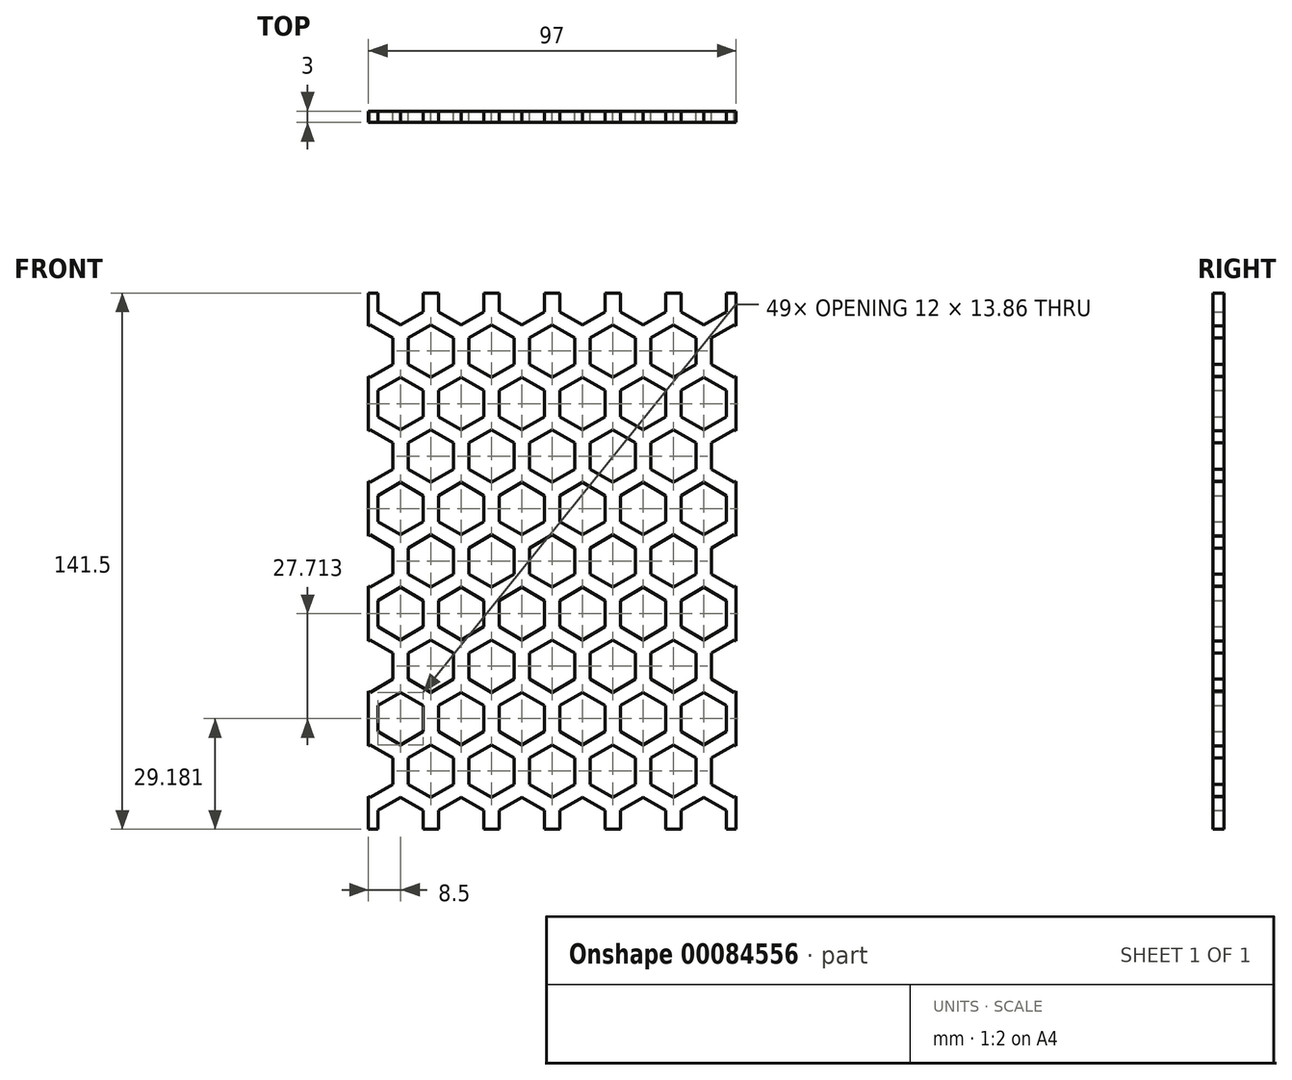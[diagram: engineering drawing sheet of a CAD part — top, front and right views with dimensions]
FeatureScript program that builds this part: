
annotation { "Feature Type Name" : "Feature", "Feature Type Description" : "" }
export const myFeature = defineFeature(function(context is Context, id is Id, definition is map)
    precondition{}
    {
        {
            var Q0;
            Q0=qCreatedBy(makeId("Front.planeOp"),FACE);
            var sketch = newSketch(context, id + "F0", { "sketchPlane" : qUnion([Q0]) });
            skLineSegment(sketch, "E0.bottom", {"start": v(48.5, -70.75) * mm, "end": v(-48.5, -70.75) * mm});
            skLineSegment(sketch, "E0.top", {"start": v(48.5, 70.75) * mm, "end": v(-48.5, 70.75) * mm});
            skLineSegment(sketch, "E0.left", {"start": v(48.5, -70.75) * mm, "end": v(48.5, 70.75) * mm});
            skLineSegment(sketch, "E0.right", {"start": v(-48.5, -70.75) * mm, "end": v(-48.5, 70.75) * mm});
            skPoint(sketch, "E0.middle", {"position": v(0, 0) * mm});
            skCircle(sketch, "E1.cCircle", {"center": v(0, 0) * mm, "radius": 6 * mm, "construction": true});
            skLineSegment(sketch, "E1.0", {"start": v(6, 3.46) * mm, "end": v(6, -3.46) * mm});
            skLineSegment(sketch, "E1.1", {"start": v(6, -3.46) * mm, "end": v(0, -6.93) * mm});
            skLineSegment(sketch, "E1.2", {"start": v(0, -6.93) * mm, "end": v(-6, -3.46) * mm});
            skLineSegment(sketch, "E1.3", {"start": v(-6, -3.46) * mm, "end": v(-6, 3.46) * mm});
            skLineSegment(sketch, "E1.4", {"start": v(-6, 3.46) * mm, "end": v(0, 6.93) * mm});
            skLineSegment(sketch, "E1.5", {"start": v(0, 6.93) * mm, "end": v(6, 3.46) * mm});
            skPoint(sketch, "E1.0.midPoint", {"position": v(6, 0) * mm});
            skLineSegment(sketch, "E2", {"start": v(0, 0) * mm, "end": v(8, 13.86) * mm, "construction": true});
            skCircle(sketch, "E3.cCircle", {"center": v(8, 13.86) * mm, "radius": 6 * mm, "construction": true});
            skLineSegment(sketch, "E3.0", {"start": v(14, 17.32) * mm, "end": v(14, 10.4) * mm});
            skLineSegment(sketch, "E3.1", {"start": v(14, 10.4) * mm, "end": v(8, 6.93) * mm});
            skLineSegment(sketch, "E3.2", {"start": v(8, 6.93) * mm, "end": v(2, 10.4) * mm});
            skLineSegment(sketch, "E3.3", {"start": v(2, 10.4) * mm, "end": v(2, 17.32) * mm});
            skLineSegment(sketch, "E3.4", {"start": v(2, 17.32) * mm, "end": v(8, 20.78) * mm});
            skLineSegment(sketch, "E3.5", {"start": v(8, 20.78) * mm, "end": v(14, 17.32) * mm});
            skPoint(sketch, "E3.0.midPoint", {"position": v(14, 13.86) * mm});
            skLineSegment(sketch, "E4.0.1.0", {"start": v(-6, 24.25) * mm, "end": v(-6, 31.18) * mm});
            skLineSegment(sketch, "E4.0.1.1", {"start": v(-6, 31.18) * mm, "end": v(0, 34.64) * mm});
            skLineSegment(sketch, "E4.0.1.2", {"start": v(0, 20.78) * mm, "end": v(-6, 24.25) * mm});
            skLineSegment(sketch, "E4.0.1.3", {"start": v(6, 24.25) * mm, "end": v(0, 20.78) * mm});
            skLineSegment(sketch, "E4.0.1.4", {"start": v(6, 31.18) * mm, "end": v(6, 24.25) * mm});
            skLineSegment(sketch, "E4.0.1.5", {"start": v(0, 34.64) * mm, "end": v(6, 31.18) * mm});
            skLineSegment(sketch, "E4.0.1.6", {"start": v(14, 38.1) * mm, "end": v(8, 34.64) * mm});
            skLineSegment(sketch, "E4.0.1.7", {"start": v(8, 34.64) * mm, "end": v(2, 38.1) * mm});
            skLineSegment(sketch, "E4.0.1.8", {"start": v(2, 38.1) * mm, "end": v(2, 45.03) * mm});
            skLineSegment(sketch, "E4.0.1.9", {"start": v(14, 45.03) * mm, "end": v(14, 38.1) * mm});
            skLineSegment(sketch, "E4.0.1.10", {"start": v(8, 48.5) * mm, "end": v(14, 45.03) * mm});
            skLineSegment(sketch, "E4.0.1.11", {"start": v(2, 45.03) * mm, "end": v(8, 48.5) * mm});
            skLineSegment(sketch, "E4.0.2.0", {"start": v(-6, 51.96) * mm, "end": v(-6, 58.89) * mm});
            skLineSegment(sketch, "E4.0.2.1", {"start": v(-6, 58.89) * mm, "end": v(0, 62.35) * mm});
            skLineSegment(sketch, "E4.0.2.2", {"start": v(0, 48.5) * mm, "end": v(-6, 51.96) * mm});
            skLineSegment(sketch, "E4.0.2.3", {"start": v(6, 51.96) * mm, "end": v(0, 48.5) * mm});
            skLineSegment(sketch, "E4.0.2.4", {"start": v(6, 58.89) * mm, "end": v(6, 51.96) * mm});
            skLineSegment(sketch, "E4.0.2.5", {"start": v(0, 62.35) * mm, "end": v(6, 58.89) * mm});
            skLineSegment(sketch, "E4.0.2.6", {"start": v(14, 65.82) * mm, "end": v(8, 62.35) * mm});
            skLineSegment(sketch, "E4.0.2.7", {"start": v(8, 62.35) * mm, "end": v(2, 65.82) * mm});
            skLineSegment(sketch, "E4.0.2.8", {"start": v(2, 65.82) * mm, "end": v(2, 72.75) * mm});
            skLineSegment(sketch, "E4.0.2.9", {"start": v(14, 72.75) * mm, "end": v(14, 65.82) * mm});
            skLineSegment(sketch, "E4.0.2.10", {"start": v(8, 76.21) * mm, "end": v(14, 72.75) * mm});
            skLineSegment(sketch, "E4.0.2.11", {"start": v(2, 72.75) * mm, "end": v(8, 76.21) * mm});
            skLineSegment(sketch, "E4.1.0.0", {"start": v(10, -3.46) * mm, "end": v(10, 3.46) * mm});
            skLineSegment(sketch, "E4.1.0.1", {"start": v(10, 3.46) * mm, "end": v(16, 6.93) * mm});
            skLineSegment(sketch, "E4.1.0.2", {"start": v(16, -6.93) * mm, "end": v(10, -3.46) * mm});
            skLineSegment(sketch, "E4.1.0.3", {"start": v(22, -3.46) * mm, "end": v(16, -6.93) * mm});
            skLineSegment(sketch, "E4.1.0.4", {"start": v(22, 3.46) * mm, "end": v(22, -3.46) * mm});
            skLineSegment(sketch, "E4.1.0.5", {"start": v(16, 6.93) * mm, "end": v(22, 3.46) * mm});
            skLineSegment(sketch, "E4.1.0.6", {"start": v(30, 10.4) * mm, "end": v(24, 6.93) * mm});
            skLineSegment(sketch, "E4.1.0.7", {"start": v(24, 6.93) * mm, "end": v(18, 10.4) * mm});
            skLineSegment(sketch, "E4.1.0.8", {"start": v(18, 10.4) * mm, "end": v(18, 17.32) * mm});
            skLineSegment(sketch, "E4.1.0.9", {"start": v(30, 17.32) * mm, "end": v(30, 10.4) * mm});
            skLineSegment(sketch, "E4.1.0.10", {"start": v(24, 20.78) * mm, "end": v(30, 17.32) * mm});
            skLineSegment(sketch, "E4.1.0.11", {"start": v(18, 17.32) * mm, "end": v(24, 20.78) * mm});
            skLineSegment(sketch, "E4.1.1.0", {"start": v(10, 24.25) * mm, "end": v(10, 31.18) * mm});
            skLineSegment(sketch, "E4.1.1.1", {"start": v(10, 31.18) * mm, "end": v(16, 34.64) * mm});
            skLineSegment(sketch, "E4.1.1.2", {"start": v(16, 20.78) * mm, "end": v(10, 24.25) * mm});
            skLineSegment(sketch, "E4.1.1.3", {"start": v(22, 24.25) * mm, "end": v(16, 20.78) * mm});
            skLineSegment(sketch, "E4.1.1.4", {"start": v(22, 31.18) * mm, "end": v(22, 24.25) * mm});
            skLineSegment(sketch, "E4.1.1.5", {"start": v(16, 34.64) * mm, "end": v(22, 31.18) * mm});
            skLineSegment(sketch, "E4.1.1.6", {"start": v(30, 38.1) * mm, "end": v(24, 34.64) * mm});
            skLineSegment(sketch, "E4.1.1.7", {"start": v(24, 34.64) * mm, "end": v(18, 38.1) * mm});
            skLineSegment(sketch, "E4.1.1.8", {"start": v(18, 38.1) * mm, "end": v(18, 45.03) * mm});
            skLineSegment(sketch, "E4.1.1.9", {"start": v(30, 45.03) * mm, "end": v(30, 38.1) * mm});
            skLineSegment(sketch, "E4.1.1.10", {"start": v(24, 48.5) * mm, "end": v(30, 45.03) * mm});
            skLineSegment(sketch, "E4.1.1.11", {"start": v(18, 45.03) * mm, "end": v(24, 48.5) * mm});
            skLineSegment(sketch, "E4.1.2.0", {"start": v(10, 51.96) * mm, "end": v(10, 58.89) * mm});
            skLineSegment(sketch, "E4.1.2.1", {"start": v(10, 58.89) * mm, "end": v(16, 62.35) * mm});
            skLineSegment(sketch, "E4.1.2.2", {"start": v(16, 48.5) * mm, "end": v(10, 51.96) * mm});
            skLineSegment(sketch, "E4.1.2.3", {"start": v(22, 51.96) * mm, "end": v(16, 48.5) * mm});
            skLineSegment(sketch, "E4.1.2.4", {"start": v(22, 58.89) * mm, "end": v(22, 51.96) * mm});
            skLineSegment(sketch, "E4.1.2.5", {"start": v(16, 62.35) * mm, "end": v(22, 58.89) * mm});
            skLineSegment(sketch, "E4.1.2.6", {"start": v(30, 65.82) * mm, "end": v(24, 62.35) * mm});
            skLineSegment(sketch, "E4.1.2.7", {"start": v(24, 62.35) * mm, "end": v(18, 65.82) * mm});
            skLineSegment(sketch, "E4.1.2.8", {"start": v(18, 65.82) * mm, "end": v(18, 72.75) * mm});
            skLineSegment(sketch, "E4.1.2.9", {"start": v(30, 72.75) * mm, "end": v(30, 65.82) * mm});
            skLineSegment(sketch, "E4.1.2.10", {"start": v(24, 76.21) * mm, "end": v(30, 72.75) * mm});
            skLineSegment(sketch, "E4.1.2.11", {"start": v(18, 72.75) * mm, "end": v(24, 76.21) * mm});
            skLineSegment(sketch, "E4.2.0.0", {"start": v(26, -3.46) * mm, "end": v(26, 3.46) * mm});
            skLineSegment(sketch, "E4.2.0.1", {"start": v(26, 3.46) * mm, "end": v(32, 6.93) * mm});
            skLineSegment(sketch, "E4.2.0.2", {"start": v(32, -6.93) * mm, "end": v(26, -3.46) * mm});
            skLineSegment(sketch, "E4.2.0.3", {"start": v(38, -3.46) * mm, "end": v(32, -6.93) * mm});
            skLineSegment(sketch, "E4.2.0.4", {"start": v(38, 3.46) * mm, "end": v(38, -3.46) * mm});
            skLineSegment(sketch, "E4.2.0.5", {"start": v(32, 6.93) * mm, "end": v(38, 3.46) * mm});
            skLineSegment(sketch, "E4.2.0.6", {"start": v(46, 10.4) * mm, "end": v(40, 6.93) * mm});
            skLineSegment(sketch, "E4.2.0.7", {"start": v(40, 6.93) * mm, "end": v(34, 10.4) * mm});
            skLineSegment(sketch, "E4.2.0.8", {"start": v(34, 10.4) * mm, "end": v(34, 17.32) * mm});
            skLineSegment(sketch, "E4.2.0.9", {"start": v(46, 17.32) * mm, "end": v(46, 10.4) * mm});
            skLineSegment(sketch, "E4.2.0.10", {"start": v(40, 20.78) * mm, "end": v(46, 17.32) * mm});
            skLineSegment(sketch, "E4.2.0.11", {"start": v(34, 17.32) * mm, "end": v(40, 20.78) * mm});
            skLineSegment(sketch, "E4.2.1.0", {"start": v(26, 24.25) * mm, "end": v(26, 31.18) * mm});
            skLineSegment(sketch, "E4.2.1.1", {"start": v(26, 31.18) * mm, "end": v(32, 34.64) * mm});
            skLineSegment(sketch, "E4.2.1.2", {"start": v(32, 20.78) * mm, "end": v(26, 24.25) * mm});
            skLineSegment(sketch, "E4.2.1.3", {"start": v(38, 24.25) * mm, "end": v(32, 20.78) * mm});
            skLineSegment(sketch, "E4.2.1.4", {"start": v(38, 31.18) * mm, "end": v(38, 24.25) * mm});
            skLineSegment(sketch, "E4.2.1.5", {"start": v(32, 34.64) * mm, "end": v(38, 31.18) * mm});
            skLineSegment(sketch, "E4.2.1.6", {"start": v(46, 38.1) * mm, "end": v(40, 34.64) * mm});
            skLineSegment(sketch, "E4.2.1.7", {"start": v(40, 34.64) * mm, "end": v(34, 38.1) * mm});
            skLineSegment(sketch, "E4.2.1.8", {"start": v(34, 38.1) * mm, "end": v(34, 45.03) * mm});
            skLineSegment(sketch, "E4.2.1.9", {"start": v(46, 45.03) * mm, "end": v(46, 38.1) * mm});
            skLineSegment(sketch, "E4.2.1.10", {"start": v(40, 48.5) * mm, "end": v(46, 45.03) * mm});
            skLineSegment(sketch, "E4.2.1.11", {"start": v(34, 45.03) * mm, "end": v(40, 48.5) * mm});
            skLineSegment(sketch, "E4.2.2.0", {"start": v(26, 51.96) * mm, "end": v(26, 58.89) * mm});
            skLineSegment(sketch, "E4.2.2.1", {"start": v(26, 58.89) * mm, "end": v(32, 62.35) * mm});
            skLineSegment(sketch, "E4.2.2.2", {"start": v(32, 48.5) * mm, "end": v(26, 51.96) * mm});
            skLineSegment(sketch, "E4.2.2.3", {"start": v(38, 51.96) * mm, "end": v(32, 48.5) * mm});
            skLineSegment(sketch, "E4.2.2.4", {"start": v(38, 58.89) * mm, "end": v(38, 51.96) * mm});
            skLineSegment(sketch, "E4.2.2.5", {"start": v(32, 62.35) * mm, "end": v(38, 58.89) * mm});
            skLineSegment(sketch, "E4.2.2.6", {"start": v(46, 65.82) * mm, "end": v(40, 62.35) * mm});
            skLineSegment(sketch, "E4.2.2.7", {"start": v(40, 62.35) * mm, "end": v(34, 65.82) * mm});
            skLineSegment(sketch, "E4.2.2.8", {"start": v(34, 65.82) * mm, "end": v(34, 72.75) * mm});
            skLineSegment(sketch, "E4.2.2.9", {"start": v(46, 72.75) * mm, "end": v(46, 65.82) * mm});
            skLineSegment(sketch, "E4.2.2.10", {"start": v(40, 76.21) * mm, "end": v(46, 72.75) * mm});
            skLineSegment(sketch, "E4.2.2.11", {"start": v(34, 72.75) * mm, "end": v(40, 76.21) * mm});
            skLineSegment(sketch, "E4.3.0.0", {"start": v(42, -3.46) * mm, "end": v(42, 3.46) * mm});
            skLineSegment(sketch, "E4.3.0.1", {"start": v(42, 3.46) * mm, "end": v(48, 6.93) * mm});
            skLineSegment(sketch, "E4.3.0.2", {"start": v(48, -6.93) * mm, "end": v(42, -3.46) * mm});
            skLineSegment(sketch, "E4.3.0.3", {"start": v(54, -3.46) * mm, "end": v(48, -6.93) * mm});
            skLineSegment(sketch, "E4.3.0.4", {"start": v(54, 3.46) * mm, "end": v(54, -3.46) * mm});
            skLineSegment(sketch, "E4.3.0.5", {"start": v(48, 6.93) * mm, "end": v(54, 3.46) * mm});
            skLineSegment(sketch, "E4.3.0.6", {"start": v(62, 10.4) * mm, "end": v(56, 6.93) * mm});
            skLineSegment(sketch, "E4.3.0.7", {"start": v(56, 6.93) * mm, "end": v(50, 10.4) * mm});
            skLineSegment(sketch, "E4.3.0.8", {"start": v(50, 10.4) * mm, "end": v(50, 17.32) * mm});
            skLineSegment(sketch, "E4.3.0.9", {"start": v(62, 17.32) * mm, "end": v(62, 10.4) * mm});
            skLineSegment(sketch, "E4.3.0.10", {"start": v(56, 20.78) * mm, "end": v(62, 17.32) * mm});
            skLineSegment(sketch, "E4.3.0.11", {"start": v(50, 17.32) * mm, "end": v(56, 20.78) * mm});
            skLineSegment(sketch, "E4.3.1.0", {"start": v(42, 24.25) * mm, "end": v(42, 31.18) * mm});
            skLineSegment(sketch, "E4.3.1.1", {"start": v(42, 31.18) * mm, "end": v(48, 34.64) * mm});
            skLineSegment(sketch, "E4.3.1.2", {"start": v(48, 20.78) * mm, "end": v(42, 24.25) * mm});
            skLineSegment(sketch, "E4.3.1.3", {"start": v(54, 24.25) * mm, "end": v(48, 20.78) * mm});
            skLineSegment(sketch, "E4.3.1.4", {"start": v(54, 31.18) * mm, "end": v(54, 24.25) * mm});
            skLineSegment(sketch, "E4.3.1.5", {"start": v(48, 34.64) * mm, "end": v(54, 31.18) * mm});
            skLineSegment(sketch, "E4.3.1.6", {"start": v(62, 38.1) * mm, "end": v(56, 34.64) * mm});
            skLineSegment(sketch, "E4.3.1.7", {"start": v(56, 34.64) * mm, "end": v(50, 38.1) * mm});
            skLineSegment(sketch, "E4.3.1.8", {"start": v(50, 38.1) * mm, "end": v(50, 45.03) * mm});
            skLineSegment(sketch, "E4.3.1.9", {"start": v(62, 45.03) * mm, "end": v(62, 38.1) * mm});
            skLineSegment(sketch, "E4.3.1.10", {"start": v(56, 48.5) * mm, "end": v(62, 45.03) * mm});
            skLineSegment(sketch, "E4.3.1.11", {"start": v(50, 45.03) * mm, "end": v(56, 48.5) * mm});
            skLineSegment(sketch, "E4.3.2.0", {"start": v(42, 51.96) * mm, "end": v(42, 58.89) * mm});
            skLineSegment(sketch, "E4.3.2.1", {"start": v(42, 58.89) * mm, "end": v(48, 62.35) * mm});
            skLineSegment(sketch, "E4.3.2.2", {"start": v(48, 48.5) * mm, "end": v(42, 51.96) * mm});
            skLineSegment(sketch, "E4.3.2.3", {"start": v(54, 51.96) * mm, "end": v(48, 48.5) * mm});
            skLineSegment(sketch, "E4.3.2.4", {"start": v(54, 58.89) * mm, "end": v(54, 51.96) * mm});
            skLineSegment(sketch, "E4.3.2.5", {"start": v(48, 62.35) * mm, "end": v(54, 58.89) * mm});
            skLineSegment(sketch, "E4.3.2.6", {"start": v(62, 65.82) * mm, "end": v(56, 62.35) * mm});
            skLineSegment(sketch, "E4.3.2.7", {"start": v(56, 62.35) * mm, "end": v(50, 65.82) * mm});
            skLineSegment(sketch, "E4.3.2.8", {"start": v(50, 65.82) * mm, "end": v(50, 72.75) * mm});
            skLineSegment(sketch, "E4.3.2.9", {"start": v(62, 72.75) * mm, "end": v(62, 65.82) * mm});
            skLineSegment(sketch, "E4.3.2.10", {"start": v(56, 76.21) * mm, "end": v(62, 72.75) * mm});
            skLineSegment(sketch, "E4.3.2.11", {"start": v(50, 72.75) * mm, "end": v(56, 76.21) * mm});
            skLineSegment(sketch, "E4.direction1", {"start": v(-6, -3.46) * mm, "end": v(10, -3.46) * mm, "construction": true});
            skLineSegment(sketch, "E4.direction2", {"start": v(-6, -3.46) * mm, "end": v(-6, 24.25) * mm, "construction": true});
            skLineSegment(sketch, "E5.MirrorCS", {"start": v(-32, 20.78) * mm, "end": v(-26, 24.25) * mm});
            skLineSegment(sketch, "E6.MirrorCS", {"start": v(-48, 20.78) * mm, "end": v(-42, 24.25) * mm});
            skLineSegment(sketch, "E7.MirrorCS", {"start": v(-2, 45.03) * mm, "end": v(-8, 48.5) * mm});
            skLineSegment(sketch, "E8.MirrorCS", {"start": v(-22, -3.46) * mm, "end": v(-16, -6.93) * mm});
            skLineSegment(sketch, "E9.MirrorCS", {"start": v(-18, 72.75) * mm, "end": v(-24, 76.21) * mm});
            skLineSegment(sketch, "E10.MirrorCS", {"start": v(-38, 24.25) * mm, "end": v(-32, 20.78) * mm});
            skLineSegment(sketch, "E11.MirrorCS", {"start": v(-40, 34.64) * mm, "end": v(-34, 38.1) * mm});
            skLineSegment(sketch, "E12.MirrorCS", {"start": v(-34, 72.75) * mm, "end": v(-40, 76.21) * mm});
            skLineSegment(sketch, "E13.MirrorCS", {"start": v(-24, 6.93) * mm, "end": v(-18, 10.4) * mm});
            skLineSegment(sketch, "E14.MirrorCS", {"start": v(-48, 34.64) * mm, "end": v(-54, 31.18) * mm});
            skLineSegment(sketch, "E15.MirrorCS", {"start": v(0, 62.35) * mm, "end": v(-6, 58.89) * mm});
            skLineSegment(sketch, "E16.MirrorCS", {"start": v(-62, 38.1) * mm, "end": v(-56, 34.64) * mm});
            skLineSegment(sketch, "E17.MirrorCS", {"start": v(-48, -6.93) * mm, "end": v(-42, -3.46) * mm});
            skLineSegment(sketch, "E18.MirrorCS", {"start": v(-18, 17.32) * mm, "end": v(-24, 20.78) * mm});
            skLineSegment(sketch, "E19.MirrorCS", {"start": v(-22, 51.96) * mm, "end": v(-16, 48.5) * mm});
            skLineSegment(sketch, "E20.MirrorCS", {"start": v(-6, 24.25) * mm, "end": v(0, 20.78) * mm});
            skLineSegment(sketch, "E21.MirrorCS", {"start": v(-34, 45.03) * mm, "end": v(-40, 48.5) * mm});
            skLineSegment(sketch, "E22.MirrorCS", {"start": v(-10, 31.18) * mm, "end": v(-16, 34.64) * mm});
            skLineSegment(sketch, "E23.MirrorCS", {"start": v(-16, 62.35) * mm, "end": v(-22, 58.89) * mm});
            skLineSegment(sketch, "E24.MirrorCS", {"start": v(-26, 58.89) * mm, "end": v(-32, 62.35) * mm});
            skLineSegment(sketch, "E25.MirrorCS", {"start": v(-16, 20.78) * mm, "end": v(-10, 24.25) * mm});
            skLineSegment(sketch, "E26.MirrorCS", {"start": v(-62, 10.4) * mm, "end": v(-56, 6.93) * mm});
            skLineSegment(sketch, "E27.MirrorCS", {"start": v(-8, 34.64) * mm, "end": v(-2, 38.1) * mm});
            skLineSegment(sketch, "E28.MirrorCS", {"start": v(-2, 72.75) * mm, "end": v(-8, 76.21) * mm});
            skLineSegment(sketch, "E29.MirrorCS", {"start": v(-10, 3.46) * mm, "end": v(-16, 6.93) * mm});
            skLineSegment(sketch, "E30.MirrorCS", {"start": v(-16, 34.64) * mm, "end": v(-22, 31.18) * mm});
            skLineSegment(sketch, "E31.MirrorCS", {"start": v(-26, 31.18) * mm, "end": v(-32, 34.64) * mm});
            skLineSegment(sketch, "E32.MirrorCS", {"start": v(-24, 62.35) * mm, "end": v(-18, 65.82) * mm});
            skLineSegment(sketch, "E33.MirrorCS", {"start": v(-34, 17.32) * mm, "end": v(-40, 20.78) * mm});
            skLineSegment(sketch, "E34.MirrorCS", {"start": v(-42, 58.89) * mm, "end": v(-48, 62.35) * mm});
            skLineSegment(sketch, "E35.MirrorCS", {"start": v(-32, 62.35) * mm, "end": v(-38, 58.89) * mm});
            skLineSegment(sketch, "E36.MirrorCS", {"start": v(-22, 24.25) * mm, "end": v(-16, 20.78) * mm});
            skLineSegment(sketch, "E37.MirrorCS", {"start": v(-8, 6.93) * mm, "end": v(-2, 10.4) * mm});
            skLineSegment(sketch, "E38.MirrorCS", {"start": v(-42, 31.18) * mm, "end": v(-48, 34.64) * mm});
            skLineSegment(sketch, "E39.MirrorCS", {"start": v(-40, 62.35) * mm, "end": v(-34, 65.82) * mm});
            skLineSegment(sketch, "E40.MirrorCS", {"start": v(-2, 17.32) * mm, "end": v(-8, 20.78) * mm});
            skLineSegment(sketch, "E41.MirrorCS", {"start": v(-10, 58.89) * mm, "end": v(-16, 62.35) * mm});
            skLineSegment(sketch, "E42.MirrorCS", {"start": v(-32, 6.93) * mm, "end": v(-38, 3.46) * mm});
            skLineSegment(sketch, "E43.MirrorCS", {"start": v(-48, 62.35) * mm, "end": v(-54, 58.89) * mm});
            skLineSegment(sketch, "E44.MirrorCS", {"start": v(-48, 6.93) * mm, "end": v(-54, 3.46) * mm});
            skLineSegment(sketch, "E45.MirrorCS", {"start": v(-62, 65.82) * mm, "end": v(-56, 62.35) * mm});
            skLineSegment(sketch, "E46.MirrorCS", {"start": v(-38, -3.46) * mm, "end": v(-32, -6.93) * mm});
            skLineSegment(sketch, "E47.MirrorCS", {"start": v(-6, -3.46) * mm, "end": v(0, -6.93) * mm});
            skLineSegment(sketch, "E48.MirrorCS", {"start": v(-56, 48.5) * mm, "end": v(-62, 45.03) * mm});
            skLineSegment(sketch, "E49.MirrorCS", {"start": v(-32, 48.5) * mm, "end": v(-26, 51.96) * mm});
            skLineSegment(sketch, "E50.MirrorCS", {"start": v(-38, 51.96) * mm, "end": v(-32, 48.5) * mm});
            skLineSegment(sketch, "E51.MirrorCS", {"start": v(0, 34.64) * mm, "end": v(-6, 31.18) * mm});
            skLineSegment(sketch, "E52.MirrorCS", {"start": v(-54, -3.46) * mm, "end": v(-48, -6.93) * mm});
            skLineSegment(sketch, "E53.MirrorCS", {"start": v(-16, 48.5) * mm, "end": v(-10, 51.96) * mm});
            skLineSegment(sketch, "E54.MirrorCS", {"start": v(-56, 76.21) * mm, "end": v(-62, 72.75) * mm});
            skLineSegment(sketch, "E55.MirrorCS", {"start": v(-42, 3.46) * mm, "end": v(-48, 6.93) * mm});
            skLineSegment(sketch, "E56.MirrorCS", {"start": v(-8, 62.35) * mm, "end": v(-2, 65.82) * mm});
            skLineSegment(sketch, "E57.MirrorCS", {"start": v(-40, 6.93) * mm, "end": v(-34, 10.4) * mm});
            skLineSegment(sketch, "E58.MirrorCS", {"start": v(-50, 65.82) * mm, "end": v(-50, 72.75) * mm});
            skLineSegment(sketch, "E59.MirrorCS", {"start": v(-54, 24.25) * mm, "end": v(-48, 20.78) * mm});
            skLineSegment(sketch, "E60.MirrorCS", {"start": v(-6, 51.96) * mm, "end": v(0, 48.5) * mm});
            skLineSegment(sketch, "E61.MirrorCS", {"start": v(-18, 45.03) * mm, "end": v(-24, 48.5) * mm});
            skLineSegment(sketch, "E62.MirrorCS", {"start": v(-54, 51.96) * mm, "end": v(-48, 48.5) * mm});
            skLineSegment(sketch, "E63.MirrorCS", {"start": v(-24, 34.64) * mm, "end": v(-18, 38.1) * mm});
            skLineSegment(sketch, "E64.MirrorCS", {"start": v(-32, -6.93) * mm, "end": v(-26, -3.46) * mm});
            skLineSegment(sketch, "E65.MirrorCS", {"start": v(-26, 3.46) * mm, "end": v(-32, 6.93) * mm});
            skLineSegment(sketch, "E66.MirrorCS", {"start": v(-32, 34.64) * mm, "end": v(-38, 31.18) * mm});
            skLineSegment(sketch, "E67.MirrorCS", {"start": v(-56, 20.78) * mm, "end": v(-62, 17.32) * mm});
            skLineSegment(sketch, "E68.MirrorCS", {"start": v(-48, 48.5) * mm, "end": v(-42, 51.96) * mm});
            skLineSegment(sketch, "E69.MirrorCS", {"start": v(-16, -6.93) * mm, "end": v(-10, -3.46) * mm});
            skLineSegment(sketch, "E70.MirrorCS", {"start": v(-16, 6.93) * mm, "end": v(-22, 3.46) * mm});
            skLineSegment(sketch, "E71.MirrorCS", {"start": v(0, 6.93) * mm, "end": v(-6, 3.46) * mm});
            skLineSegment(sketch, "E72.MirrorCS", {"start": v(0, 0) * mm, "end": v(-8, 13.86) * mm, "construction": true});
            skLineSegment(sketch, "E73.MirrorCS", {"start": v(-6, 3.46) * mm, "end": v(-6, -3.46) * mm});
            skLineSegment(sketch, "E74.MirrorCS", {"start": v(-14, 10.4) * mm, "end": v(-8, 6.93) * mm});
            skLineSegment(sketch, "E75.MirrorCS", {"start": v(-14, 17.32) * mm, "end": v(-14, 10.4) * mm});
            skLineSegment(sketch, "E76.MirrorCS", {"start": v(-2, 10.4) * mm, "end": v(-2, 17.32) * mm});
            skCircle(sketch, "E77.MirrorC", {"center": v(-8, 13.86) * mm, "radius": 6 * mm, "construction": true});
            skLineSegment(sketch, "E78.MirrorCS", {"start": v(-46, 65.82) * mm, "end": v(-40, 62.35) * mm});
            skLineSegment(sketch, "E79.MirrorCS", {"start": v(-8, 48.5) * mm, "end": v(-14, 45.03) * mm});
            skLineSegment(sketch, "E80.MirrorCS", {"start": v(-30, 38.1) * mm, "end": v(-24, 34.64) * mm});
            skLineSegment(sketch, "E81.MirrorCS", {"start": v(-24, 76.21) * mm, "end": v(-30, 72.75) * mm});
            skLineSegment(sketch, "E82.MirrorCS", {"start": v(-46, 72.75) * mm, "end": v(-46, 65.82) * mm});
            skLineSegment(sketch, "E83.MirrorCS", {"start": v(-30, 45.03) * mm, "end": v(-30, 38.1) * mm});
            skPoint(sketch, "E84.MirrorP", {"position": v(-6, 0) * mm});
            skLineSegment(sketch, "E85.MirrorCS", {"start": v(-24, 48.5) * mm, "end": v(-30, 45.03) * mm});
            skLineSegment(sketch, "E86.MirrorCS", {"start": v(-46, 38.1) * mm, "end": v(-40, 34.64) * mm});
            skLineSegment(sketch, "E87.MirrorCS", {"start": v(-8, 20.78) * mm, "end": v(-14, 17.32) * mm});
            skLineSegment(sketch, "E88.MirrorCS", {"start": v(-56, 62.35) * mm, "end": v(-50, 65.82) * mm});
            skLineSegment(sketch, "E89.MirrorCS", {"start": v(-24, 20.78) * mm, "end": v(-30, 17.32) * mm});
            skLineSegment(sketch, "E90.MirrorCS", {"start": v(-50, 72.75) * mm, "end": v(-56, 76.21) * mm});
            skLineSegment(sketch, "E91.MirrorCS", {"start": v(-18, 10.4) * mm, "end": v(-18, 17.32) * mm});
            skLineSegment(sketch, "E92.MirrorCS", {"start": v(-54, 31.18) * mm, "end": v(-54, 24.25) * mm});
            skLineSegment(sketch, "E93.MirrorCS", {"start": v(-6, 31.18) * mm, "end": v(-6, 24.25) * mm});
            skLineSegment(sketch, "E94.MirrorCS", {"start": v(-10, 24.25) * mm, "end": v(-10, 31.18) * mm});
            skLineSegment(sketch, "E95.MirrorCS", {"start": v(-22, 58.89) * mm, "end": v(-22, 51.96) * mm});
            skLineSegment(sketch, "E96.MirrorCS", {"start": v(-26, 51.96) * mm, "end": v(-26, 58.89) * mm});
            skLineSegment(sketch, "E97.MirrorCS", {"start": v(-62, 45.03) * mm, "end": v(-62, 38.1) * mm});
            skLineSegment(sketch, "E98.MirrorCS", {"start": v(-8, 76.21) * mm, "end": v(-14, 72.75) * mm});
            skLineSegment(sketch, "E99.MirrorCS", {"start": v(-30, 65.82) * mm, "end": v(-24, 62.35) * mm});
            skLineSegment(sketch, "E100.MirrorCS", {"start": v(-14, 45.03) * mm, "end": v(-14, 38.1) * mm});
            skLineSegment(sketch, "E101.MirrorCS", {"start": v(-62, 17.32) * mm, "end": v(-62, 10.4) * mm});
            skLineSegment(sketch, "E102.MirrorCS", {"start": v(-30, 72.75) * mm, "end": v(-30, 65.82) * mm});
            skLineSegment(sketch, "E103.MirrorCS", {"start": v(-22, 31.18) * mm, "end": v(-22, 24.25) * mm});
            skLineSegment(sketch, "E104.MirrorCS", {"start": v(-38, 58.89) * mm, "end": v(-38, 51.96) * mm});
            skLineSegment(sketch, "E105.MirrorCS", {"start": v(-50, 10.4) * mm, "end": v(-50, 17.32) * mm});
            skLineSegment(sketch, "E106.MirrorCS", {"start": v(-2, 38.1) * mm, "end": v(-2, 45.03) * mm});
            skLineSegment(sketch, "E107.MirrorCS", {"start": v(-10, -3.46) * mm, "end": v(-10, 3.46) * mm});
            skLineSegment(sketch, "E108.MirrorCS", {"start": v(-42, 51.96) * mm, "end": v(-42, 58.89) * mm});
            skLineSegment(sketch, "E109.MirrorCS", {"start": v(-18, 65.82) * mm, "end": v(-18, 72.75) * mm});
            skLineSegment(sketch, "E110.MirrorCS", {"start": v(-50, 45.03) * mm, "end": v(-56, 48.5) * mm});
            skLineSegment(sketch, "E111.MirrorCS", {"start": v(-30, 17.32) * mm, "end": v(-30, 10.4) * mm});
            skLineSegment(sketch, "E112.MirrorCS", {"start": v(-46, 45.03) * mm, "end": v(-46, 38.1) * mm});
            skLineSegment(sketch, "E113.MirrorCS", {"start": v(-34, 65.82) * mm, "end": v(-34, 72.75) * mm});
            skLineSegment(sketch, "E114.MirrorCS", {"start": v(-54, 58.89) * mm, "end": v(-54, 51.96) * mm});
            skLineSegment(sketch, "E115.MirrorCS", {"start": v(-42, 24.25) * mm, "end": v(-42, 31.18) * mm});
            skLineSegment(sketch, "E116.MirrorCS", {"start": v(-26, -3.46) * mm, "end": v(-26, 3.46) * mm});
            skLineSegment(sketch, "E117.MirrorCS", {"start": v(-50, 38.1) * mm, "end": v(-50, 45.03) * mm});
            skLineSegment(sketch, "E118.MirrorCS", {"start": v(-42, -3.46) * mm, "end": v(-42, 3.46) * mm});
            skLineSegment(sketch, "E119.MirrorCS", {"start": v(-46, 10.4) * mm, "end": v(-40, 6.93) * mm});
            skLineSegment(sketch, "E120.MirrorCS", {"start": v(-6, 58.89) * mm, "end": v(-6, 51.96) * mm});
            skLineSegment(sketch, "E121.MirrorCS", {"start": v(-38, 3.46) * mm, "end": v(-38, -3.46) * mm});
            skLineSegment(sketch, "E122.MirrorCS", {"start": v(-38, 31.18) * mm, "end": v(-38, 24.25) * mm});
            skLineSegment(sketch, "E123.MirrorCS", {"start": v(-22, 3.46) * mm, "end": v(-22, -3.46) * mm});
            skLineSegment(sketch, "E124.MirrorCS", {"start": v(-50, 17.32) * mm, "end": v(-56, 20.78) * mm});
            skLineSegment(sketch, "E125.MirrorCS", {"start": v(-54, 3.46) * mm, "end": v(-54, -3.46) * mm});
            skLineSegment(sketch, "E126.MirrorCS", {"start": v(-46, 17.32) * mm, "end": v(-46, 10.4) * mm});
            skLineSegment(sketch, "E127.MirrorCS", {"start": v(-2, 65.82) * mm, "end": v(-2, 72.75) * mm});
            skLineSegment(sketch, "E128.MirrorCS", {"start": v(-40, 76.21) * mm, "end": v(-46, 72.75) * mm});
            skLineSegment(sketch, "E129.MirrorCS", {"start": v(-40, 20.78) * mm, "end": v(-46, 17.32) * mm});
            skLineSegment(sketch, "E130.MirrorCS", {"start": v(-14, 38.1) * mm, "end": v(-8, 34.64) * mm});
            skLineSegment(sketch, "E131.MirrorCS", {"start": v(-56, 6.93) * mm, "end": v(-50, 10.4) * mm});
            skLineSegment(sketch, "E132.MirrorCS", {"start": v(-14, 72.75) * mm, "end": v(-14, 65.82) * mm});
            skLineSegment(sketch, "E133.MirrorCS", {"start": v(-34, 10.4) * mm, "end": v(-34, 17.32) * mm});
            skLineSegment(sketch, "E134.MirrorCS", {"start": v(-34, 38.1) * mm, "end": v(-34, 45.03) * mm});
            skLineSegment(sketch, "E135.MirrorCS", {"start": v(-10, 51.96) * mm, "end": v(-10, 58.89) * mm});
            skLineSegment(sketch, "E136.MirrorCS", {"start": v(-40, 48.5) * mm, "end": v(-46, 45.03) * mm});
            skLineSegment(sketch, "E137.MirrorCS", {"start": v(-62, 72.75) * mm, "end": v(-62, 65.82) * mm});
            skLineSegment(sketch, "E138.MirrorCS", {"start": v(-56, 34.64) * mm, "end": v(-50, 38.1) * mm});
            skPoint(sketch, "E139.MirrorP", {"position": v(-14, 13.86) * mm});
            skLineSegment(sketch, "E140.MirrorCS", {"start": v(-18, 38.1) * mm, "end": v(-18, 45.03) * mm});
            skLineSegment(sketch, "E141.MirrorCS", {"start": v(-30, 10.4) * mm, "end": v(-24, 6.93) * mm});
            skLineSegment(sketch, "E142.MirrorCS", {"start": v(-26, 24.25) * mm, "end": v(-26, 31.18) * mm});
            skLineSegment(sketch, "E143.MirrorCS", {"start": v(-14, 65.82) * mm, "end": v(-8, 62.35) * mm});
            skLineSegment(sketch, "E144.MirrorCS", {"start": v(0, -20.78) * mm, "end": v(-6, -24.25) * mm});
            skLineSegment(sketch, "E145.MirrorCS", {"start": v(-6, -31.18) * mm, "end": v(0, -34.64) * mm});
            skLineSegment(sketch, "E146.MirrorCS", {"start": v(-6, -51.96) * mm, "end": v(0, -48.5) * mm});
            skLineSegment(sketch, "E147.MirrorCS", {"start": v(-6, -58.89) * mm, "end": v(0, -62.35) * mm});
            skLineSegment(sketch, "E148.MirrorCS", {"start": v(0, -62.35) * mm, "end": v(-6, -58.89) * mm});
            skLineSegment(sketch, "E149.MirrorCS", {"start": v(0, -48.5) * mm, "end": v(-6, -51.96) * mm});
            skLineSegment(sketch, "E150.MirrorCS", {"start": v(-6, -24.25) * mm, "end": v(0, -20.78) * mm});
            skLineSegment(sketch, "E151.MirrorCS", {"start": v(0, -34.64) * mm, "end": v(-6, -31.18) * mm});
            skLineSegment(sketch, "E152.MirrorCS", {"start": v(56, -20.78) * mm, "end": v(62, -17.32) * mm});
            skLineSegment(sketch, "E153.MirrorCS", {"start": v(30, -38.1) * mm, "end": v(24, -34.64) * mm});
            skLineSegment(sketch, "E154.MirrorCS", {"start": v(24, -76.21) * mm, "end": v(30, -72.75) * mm});
            skLineSegment(sketch, "E155.MirrorCS", {"start": v(14, -10.4) * mm, "end": v(8, -6.93) * mm});
            skLineSegment(sketch, "E156.MirrorCS", {"start": v(-14, -38.1) * mm, "end": v(-8, -34.64) * mm});
            skLineSegment(sketch, "E157.MirrorCS", {"start": v(56, -76.21) * mm, "end": v(62, -72.75) * mm});
            skLineSegment(sketch, "E158.MirrorCS", {"start": v(40, -48.5) * mm, "end": v(46, -45.03) * mm});
            skLineSegment(sketch, "E159.MirrorCS", {"start": v(46, -10.4) * mm, "end": v(40, -6.93) * mm});
            skLineSegment(sketch, "E160.MirrorCS", {"start": v(14, -65.82) * mm, "end": v(8, -62.35) * mm});
            skLineSegment(sketch, "E161.MirrorCS", {"start": v(-8, -48.5) * mm, "end": v(-14, -45.03) * mm});
            skLineSegment(sketch, "E162.MirrorCS", {"start": v(-30, -38.1) * mm, "end": v(-24, -34.64) * mm});
            skLineSegment(sketch, "E163.MirrorCS", {"start": v(-24, -62.35) * mm, "end": v(-18, -65.82) * mm});
            skLineSegment(sketch, "E164.MirrorCS", {"start": v(24, -48.5) * mm, "end": v(30, -45.03) * mm});
            skLineSegment(sketch, "E165.MirrorCS", {"start": v(40, -76.21) * mm, "end": v(46, -72.75) * mm});
            skLineSegment(sketch, "E166.MirrorCS", {"start": v(-14, -65.82) * mm, "end": v(-8, -62.35) * mm});
            skLineSegment(sketch, "E167.MirrorCS", {"start": v(-62, -65.82) * mm, "end": v(-56, -62.35) * mm});
            skLineSegment(sketch, "E168.MirrorCS", {"start": v(8, -20.78) * mm, "end": v(14, -17.32) * mm});
            skLineSegment(sketch, "E169.MirrorCS", {"start": v(-2, -72.75) * mm, "end": v(-8, -76.21) * mm});
            skLineSegment(sketch, "E170.MirrorCS", {"start": v(42, -31.18) * mm, "end": v(48, -34.64) * mm});
            skLineSegment(sketch, "E171.MirrorCS", {"start": v(-40, -34.64) * mm, "end": v(-34, -38.1) * mm});
            skLineSegment(sketch, "E172.MirrorCS", {"start": v(-50, -65.82) * mm, "end": v(-50, -72.75) * mm});
            skLineSegment(sketch, "E173.MirrorCS", {"start": v(-62, -10.4) * mm, "end": v(-56, -6.93) * mm});
            skLineSegment(sketch, "E174.MirrorCS", {"start": v(-40, -6.93) * mm, "end": v(-34, -10.4) * mm});
            skLineSegment(sketch, "E175.MirrorCS", {"start": v(8, -48.5) * mm, "end": v(14, -45.03) * mm});
            skLineSegment(sketch, "E176.MirrorCS", {"start": v(46, -38.1) * mm, "end": v(40, -34.64) * mm});
            skLineSegment(sketch, "E177.MirrorCS", {"start": v(48, -34.64) * mm, "end": v(54, -31.18) * mm});
            skLineSegment(sketch, "E178.MirrorCS", {"start": v(-24, -34.64) * mm, "end": v(-18, -38.1) * mm});
            skLineSegment(sketch, "E179.MirrorCS", {"start": v(14, -38.1) * mm, "end": v(8, -34.64) * mm});
            skLineSegment(sketch, "E180.MirrorCS", {"start": v(8, -76.21) * mm, "end": v(14, -72.75) * mm});
            skLineSegment(sketch, "E181.MirrorCS", {"start": v(-22, -51.96) * mm, "end": v(-16, -48.5) * mm});
            skLineSegment(sketch, "E182.MirrorCS", {"start": v(-8, -6.93) * mm, "end": v(-2, -10.4) * mm});
            skLineSegment(sketch, "E183.MirrorCS", {"start": v(-32, -20.78) * mm, "end": v(-26, -24.25) * mm});
            skLineSegment(sketch, "E184.MirrorCS", {"start": v(-46, -38.1) * mm, "end": v(-40, -34.64) * mm});
            skLineSegment(sketch, "E185.MirrorCS", {"start": v(-24, -48.5) * mm, "end": v(-30, -45.03) * mm});
            skLineSegment(sketch, "E186.MirrorCS", {"start": v(16, -20.78) * mm, "end": v(10, -24.25) * mm});
            skLineSegment(sketch, "E187.MirrorCS", {"start": v(42, -58.89) * mm, "end": v(48, -62.35) * mm});
            skLineSegment(sketch, "E188.MirrorCS", {"start": v(-46, -65.82) * mm, "end": v(-40, -62.35) * mm});
            skLineSegment(sketch, "E189.MirrorCS", {"start": v(-40, -48.5) * mm, "end": v(-46, -45.03) * mm});
            skLineSegment(sketch, "E190.MirrorCS", {"start": v(-2, -10.4) * mm, "end": v(-2, -17.32) * mm});
            skLineSegment(sketch, "E191.MirrorCS", {"start": v(26, -58.89) * mm, "end": v(32, -62.35) * mm});
            skLineSegment(sketch, "E192.MirrorCS", {"start": v(30, -10.4) * mm, "end": v(24, -6.93) * mm});
            skLineSegment(sketch, "E193.MirrorCS", {"start": v(54, -24.25) * mm, "end": v(48, -20.78) * mm});
            skLineSegment(sketch, "E194.MirrorCS", {"start": v(10, -58.89) * mm, "end": v(16, -62.35) * mm});
            skLineSegment(sketch, "E195.MirrorCS", {"start": v(-56, -48.5) * mm, "end": v(-62, -45.03) * mm});
            skLineSegment(sketch, "E196.MirrorCS", {"start": v(-30, -65.82) * mm, "end": v(-24, -62.35) * mm});
            skLineSegment(sketch, "E197.MirrorCS", {"start": v(-8, -76.21) * mm, "end": v(-14, -72.75) * mm});
            skLineSegment(sketch, "E198.MirrorCS", {"start": v(-2, -45.03) * mm, "end": v(-8, -48.5) * mm});
            skLineSegment(sketch, "E199.MirrorCS", {"start": v(62, -65.82) * mm, "end": v(56, -62.35) * mm});
            skLineSegment(sketch, "E200.MirrorCS", {"start": v(-24, -76.21) * mm, "end": v(-30, -72.75) * mm});
            skLineSegment(sketch, "E201.MirrorCS", {"start": v(-42, -31.18) * mm, "end": v(-48, -34.64) * mm});
            skLineSegment(sketch, "E202.MirrorCS", {"start": v(-14, -10.4) * mm, "end": v(-8, -6.93) * mm});
            skLineSegment(sketch, "E203.MirrorCS", {"start": v(-34, -72.75) * mm, "end": v(-40, -76.21) * mm});
            skLineSegment(sketch, "E204.MirrorCS", {"start": v(48, -20.78) * mm, "end": v(42, -24.25) * mm});
            skLineSegment(sketch, "E205.MirrorCS", {"start": v(62, -38.1) * mm, "end": v(56, -34.64) * mm});
            skLineSegment(sketch, "E206.MirrorCS", {"start": v(-18, -72.75) * mm, "end": v(-24, -76.21) * mm});
            skLineSegment(sketch, "E207.MirrorCS", {"start": v(32, -20.78) * mm, "end": v(26, -24.25) * mm});
            skLineSegment(sketch, "E208.MirrorCS", {"start": v(-48, -20.78) * mm, "end": v(-42, -24.25) * mm});
            skLineSegment(sketch, "E209.MirrorCS", {"start": v(30, -65.82) * mm, "end": v(24, -62.35) * mm});
            skLineSegment(sketch, "E210.MirrorCS", {"start": v(-40, -62.35) * mm, "end": v(-34, -65.82) * mm});
            skLineSegment(sketch, "E211.MirrorCS", {"start": v(-8, -34.64) * mm, "end": v(-2, -38.1) * mm});
            skLineSegment(sketch, "E212.MirrorCS", {"start": v(-30, -10.4) * mm, "end": v(-24, -6.93) * mm});
            skLineSegment(sketch, "E213.MirrorCS", {"start": v(-14, -17.32) * mm, "end": v(-14, -10.4) * mm});
            skLineSegment(sketch, "E214.MirrorCS", {"start": v(48, -62.35) * mm, "end": v(54, -58.89) * mm});
            skLineSegment(sketch, "E215.MirrorCS", {"start": v(-18, -17.32) * mm, "end": v(-24, -20.78) * mm});
            skLineSegment(sketch, "E216.MirrorCS", {"start": v(-56, -76.21) * mm, "end": v(-62, -72.75) * mm});
            skLineSegment(sketch, "E217.MirrorCS", {"start": v(-18, -45.03) * mm, "end": v(-24, -48.5) * mm});
            skLineSegment(sketch, "E218.MirrorCS", {"start": v(-24, -6.93) * mm, "end": v(-18, -10.4) * mm});
            skLineSegment(sketch, "E219.MirrorCS", {"start": v(-62, -38.1) * mm, "end": v(-56, -34.64) * mm});
            skLineSegment(sketch, "E220.MirrorCS", {"start": v(-40, -20.78) * mm, "end": v(-46, -17.32) * mm});
            skLineSegment(sketch, "E221.MirrorCS", {"start": v(-40, -76.21) * mm, "end": v(-46, -72.75) * mm});
            skLineSegment(sketch, "E222.MirrorCS", {"start": v(50, -65.82) * mm, "end": v(50, -72.75) * mm});
            skLineSegment(sketch, "E223.MirrorCS", {"start": v(-26, -31.18) * mm, "end": v(-32, -34.64) * mm});
            skLineSegment(sketch, "E224.MirrorCS", {"start": v(16, -48.5) * mm, "end": v(10, -51.96) * mm});
            skLineSegment(sketch, "E225.MirrorCS", {"start": v(24, -20.78) * mm, "end": v(30, -17.32) * mm});
            skLineSegment(sketch, "E226.MirrorCS", {"start": v(-2, -17.32) * mm, "end": v(-8, -20.78) * mm});
            skLineSegment(sketch, "E227.MirrorCS", {"start": v(-22, -24.25) * mm, "end": v(-16, -20.78) * mm});
            skLineSegment(sketch, "E228.MirrorCS", {"start": v(-56, -20.78) * mm, "end": v(-62, -17.32) * mm});
            skLineSegment(sketch, "E229.MirrorCS", {"start": v(26, -31.18) * mm, "end": v(32, -34.64) * mm});
            skLineSegment(sketch, "E230.MirrorCS", {"start": v(-16, -62.35) * mm, "end": v(-22, -58.89) * mm});
            skLineSegment(sketch, "E231.MirrorCS", {"start": v(-16, -34.64) * mm, "end": v(-22, -31.18) * mm});
            skLineSegment(sketch, "E232.MirrorCS", {"start": v(-46, -10.4) * mm, "end": v(-40, -6.93) * mm});
            skLineSegment(sketch, "E233.MirrorCS", {"start": v(56, -48.5) * mm, "end": v(62, -45.03) * mm});
            skLineSegment(sketch, "E234.MirrorCS", {"start": v(-8, -20.78) * mm, "end": v(-14, -17.32) * mm});
            skLineSegment(sketch, "E235.MirrorCS", {"start": v(46, -65.82) * mm, "end": v(40, -62.35) * mm});
            skLineSegment(sketch, "E236.MirrorCS", {"start": v(54, -51.96) * mm, "end": v(48, -48.5) * mm});
            skLineSegment(sketch, "E237.MirrorCS", {"start": v(48, -48.5) * mm, "end": v(42, -51.96) * mm});
            skLineSegment(sketch, "E238.MirrorCS", {"start": v(-34, -45.03) * mm, "end": v(-40, -48.5) * mm});
            skLineSegment(sketch, "E239.MirrorCS", {"start": v(32, -48.5) * mm, "end": v(26, -51.96) * mm});
            skLineSegment(sketch, "E240.MirrorCS", {"start": v(62, -10.4) * mm, "end": v(56, -6.93) * mm});
            skLineSegment(sketch, "E241.MirrorCS", {"start": v(10, -31.18) * mm, "end": v(16, -34.64) * mm});
            skLineSegment(sketch, "E242.MirrorCS", {"start": v(40, -20.78) * mm, "end": v(46, -17.32) * mm});
            skLineSegment(sketch, "E243.MirrorCS", {"start": v(-8, -62.35) * mm, "end": v(-2, -65.82) * mm});
            skLineSegment(sketch, "E244.MirrorCS", {"start": v(-48, -48.5) * mm, "end": v(-42, -51.96) * mm});
            skLineSegment(sketch, "E245.MirrorCS", {"start": v(-26, -58.89) * mm, "end": v(-32, -62.35) * mm});
            skLineSegment(sketch, "E246.MirrorCS", {"start": v(-24, -20.78) * mm, "end": v(-30, -17.32) * mm});
            skLineSegment(sketch, "E247.MirrorCS", {"start": v(8, -6.93) * mm, "end": v(2, -10.4) * mm});
            skLineSegment(sketch, "E248.MirrorCS", {"start": v(-32, -48.5) * mm, "end": v(-26, -51.96) * mm});
            skLineSegment(sketch, "E249.MirrorCS", {"start": v(-34, -17.32) * mm, "end": v(-40, -20.78) * mm});
            skLineSegment(sketch, "E250.MirrorCS", {"start": v(-42, -58.89) * mm, "end": v(-48, -62.35) * mm});
            skLineSegment(sketch, "E251.MirrorCS", {"start": v(-10, -24.25) * mm, "end": v(-10, -31.18) * mm});
            skLineSegment(sketch, "E252.MirrorCS", {"start": v(-18, -10.4) * mm, "end": v(-18, -17.32) * mm});
            skLineSegment(sketch, "E253.MirrorCS", {"start": v(-6, -31.18) * mm, "end": v(-6, -24.25) * mm});
            skCircle(sketch, "E254.MirrorC", {"center": v(-8, -13.86) * mm, "radius": 6 * mm, "construction": true});
            skLineSegment(sketch, "E255.MirrorCS", {"start": v(-6, -51.96) * mm, "end": v(-6, -58.89) * mm});
            skLineSegment(sketch, "E256.MirrorCS", {"start": v(2, -17.32) * mm, "end": v(8, -20.78) * mm});
            skLineSegment(sketch, "E257.MirrorCS", {"start": v(14, -17.32) * mm, "end": v(14, -10.4) * mm});
            skLineSegment(sketch, "E258.MirrorCS", {"start": v(0, 0) * mm, "end": v(8, -13.86) * mm, "construction": true});
            skLineSegment(sketch, "E259.MirrorCS", {"start": v(48.5, 70.75) * mm, "end": v(48.5, -70.75) * mm});
            skPoint(sketch, "E260.MirrorP", {"position": v(-14, -13.86) * mm});
            skLineSegment(sketch, "E261.MirrorCS", {"start": v(-46, -45.03) * mm, "end": v(-46, -38.1) * mm});
            skLineSegment(sketch, "E262.MirrorCS", {"start": v(54, -31.18) * mm, "end": v(54, -24.25) * mm});
            skLineSegment(sketch, "E263.MirrorCS", {"start": v(34, -38.1) * mm, "end": v(34, -45.03) * mm});
            skLineSegment(sketch, "E264.MirrorCS", {"start": v(10, -51.96) * mm, "end": v(10, -58.89) * mm});
            skLineSegment(sketch, "E265.MirrorCS", {"start": v(6, -58.89) * mm, "end": v(6, -51.96) * mm});
            skLineSegment(sketch, "E266.MirrorCS", {"start": v(-34, -65.82) * mm, "end": v(-34, -72.75) * mm});
            skLineSegment(sketch, "E267.MirrorCS", {"start": v(46, -45.03) * mm, "end": v(46, -38.1) * mm});
            skLineSegment(sketch, "E268.MirrorCS", {"start": v(-6, -24.25) * mm, "end": v(-6, -31.18) * mm});
            skLineSegment(sketch, "E269.MirrorCS", {"start": v(-48, -34.64) * mm, "end": v(-54, -31.18) * mm});
            skLineSegment(sketch, "E270.MirrorCS", {"start": v(18, -45.03) * mm, "end": v(24, -48.5) * mm});
            skLineSegment(sketch, "E271.MirrorCS", {"start": v(56, -62.35) * mm, "end": v(50, -65.82) * mm});
            skLineSegment(sketch, "E272.MirrorCS", {"start": v(32, -34.64) * mm, "end": v(38, -31.18) * mm});
            skLineSegment(sketch, "E273.MirrorCS", {"start": v(-54, -31.18) * mm, "end": v(-54, -24.25) * mm});
            skLineSegment(sketch, "E274.MirrorCS", {"start": v(-48, -62.35) * mm, "end": v(-54, -58.89) * mm});
            skLineSegment(sketch, "E275.MirrorCS", {"start": v(-42, -51.96) * mm, "end": v(-42, -58.89) * mm});
            skLineSegment(sketch, "E276.MirrorCS", {"start": v(54, -58.89) * mm, "end": v(54, -51.96) * mm});
            skLineSegment(sketch, "E277.MirrorCS", {"start": v(18, -38.1) * mm, "end": v(18, -45.03) * mm});
            skLineSegment(sketch, "E278.MirrorCS", {"start": v(18, -72.75) * mm, "end": v(24, -76.21) * mm});
            skLineSegment(sketch, "E279.MirrorCS", {"start": v(24, -34.64) * mm, "end": v(18, -38.1) * mm});
            skLineSegment(sketch, "E280.MirrorCS", {"start": v(-38, -24.25) * mm, "end": v(-32, -20.78) * mm});
            skLineSegment(sketch, "E281.MirrorCS", {"start": v(-18, -38.1) * mm, "end": v(-18, -45.03) * mm});
            skLineSegment(sketch, "E282.MirrorCS", {"start": v(40, -62.35) * mm, "end": v(34, -65.82) * mm});
            skLineSegment(sketch, "E283.MirrorCS", {"start": v(-16, -20.78) * mm, "end": v(-10, -24.25) * mm});
            skLineSegment(sketch, "E284.MirrorCS", {"start": v(-50, -72.75) * mm, "end": v(-56, -76.21) * mm});
            skLineSegment(sketch, "E285.MirrorCS", {"start": v(-56, -34.64) * mm, "end": v(-50, -38.1) * mm});
            skLineSegment(sketch, "E286.MirrorCS", {"start": v(-10, -58.89) * mm, "end": v(-16, -62.35) * mm});
            skLineSegment(sketch, "E287.MirrorCS", {"start": v(34, -72.75) * mm, "end": v(40, -76.21) * mm});
            skLineSegment(sketch, "E288.MirrorCS", {"start": v(0, -62.35) * mm, "end": v(6, -58.89) * mm});
            skLineSegment(sketch, "E289.MirrorCS", {"start": v(30, -17.32) * mm, "end": v(30, -10.4) * mm});
            skLineSegment(sketch, "E290.MirrorCS", {"start": v(-62, -45.03) * mm, "end": v(-62, -38.1) * mm});
            skLineSegment(sketch, "E291.MirrorCS", {"start": v(38, -58.89) * mm, "end": v(38, -51.96) * mm});
            skLineSegment(sketch, "E292.MirrorCS", {"start": v(-50, -38.1) * mm, "end": v(-50, -45.03) * mm});
            skLineSegment(sketch, "E293.MirrorCS", {"start": v(34, -17.32) * mm, "end": v(40, -20.78) * mm});
            skLineSegment(sketch, "E294.MirrorCS", {"start": v(56, -6.93) * mm, "end": v(50, -10.4) * mm});
            skLineSegment(sketch, "E295.MirrorCS", {"start": v(24, -62.35) * mm, "end": v(18, -65.82) * mm});
            skLineSegment(sketch, "E296.MirrorCS", {"start": v(8, -34.64) * mm, "end": v(2, -38.1) * mm});
            skLineSegment(sketch, "E297.MirrorCS", {"start": v(62, -45.03) * mm, "end": v(62, -38.1) * mm});
            skLineSegment(sketch, "E298.MirrorCS", {"start": v(22, -51.96) * mm, "end": v(16, -48.5) * mm});
            skLineSegment(sketch, "E299.MirrorCS", {"start": v(2, -65.82) * mm, "end": v(2, -72.75) * mm});
            skLineSegment(sketch, "E300.MirrorCS", {"start": v(16, -62.35) * mm, "end": v(22, -58.89) * mm});
            skLineSegment(sketch, "E301.MirrorCS", {"start": v(50, -38.1) * mm, "end": v(50, -45.03) * mm});
            skLineSegment(sketch, "E302.MirrorCS", {"start": v(-32, -34.64) * mm, "end": v(-38, -31.18) * mm});
            skLineSegment(sketch, "E303.MirrorCS", {"start": v(-50, -10.4) * mm, "end": v(-50, -17.32) * mm});
            skLineSegment(sketch, "E304.MirrorCS", {"start": v(-38, -51.96) * mm, "end": v(-32, -48.5) * mm});
            skLineSegment(sketch, "E305.MirrorCS", {"start": v(62, -17.32) * mm, "end": v(62, -10.4) * mm});
            skLineSegment(sketch, "E306.MirrorCS", {"start": v(-18, -65.82) * mm, "end": v(-18, -72.75) * mm});
            skLineSegment(sketch, "E307.MirrorCS", {"start": v(-2, -65.82) * mm, "end": v(-2, -72.75) * mm});
            skLineSegment(sketch, "E308.MirrorCS", {"start": v(-30, -17.32) * mm, "end": v(-30, -10.4) * mm});
            skLineSegment(sketch, "E309.MirrorCS", {"start": v(16, -34.64) * mm, "end": v(22, -31.18) * mm});
            skLineSegment(sketch, "E310.MirrorCS", {"start": v(-6, -58.89) * mm, "end": v(-6, -51.96) * mm});
            skLineSegment(sketch, "E311.MirrorCS", {"start": v(-26, -24.25) * mm, "end": v(-26, -31.18) * mm});
            skLineSegment(sketch, "E312.MirrorCS", {"start": v(24, -6.93) * mm, "end": v(18, -10.4) * mm});
            skLineSegment(sketch, "E313.MirrorCS", {"start": v(62, -72.75) * mm, "end": v(62, -65.82) * mm});
            skLineSegment(sketch, "E314.MirrorCS", {"start": v(-10, -51.96) * mm, "end": v(-10, -58.89) * mm});
            skLineSegment(sketch, "E315.MirrorCS", {"start": v(-50, -17.32) * mm, "end": v(-56, -20.78) * mm});
            skLineSegment(sketch, "E316.MirrorCS", {"start": v(46, -72.75) * mm, "end": v(46, -65.82) * mm});
            skLineSegment(sketch, "E317.MirrorCS", {"start": v(10, -24.25) * mm, "end": v(10, -31.18) * mm});
            skLineSegment(sketch, "E318.MirrorCS", {"start": v(-22, -31.18) * mm, "end": v(-22, -24.25) * mm});
            skLineSegment(sketch, "E319.MirrorCS", {"start": v(-32, -62.35) * mm, "end": v(-38, -58.89) * mm});
            skLineSegment(sketch, "E320.MirrorCS", {"start": v(0, -34.64) * mm, "end": v(6, -31.18) * mm});
            skLineSegment(sketch, "E321.MirrorCS", {"start": v(32, -62.35) * mm, "end": v(38, -58.89) * mm});
            skLineSegment(sketch, "E322.MirrorCS", {"start": v(18, -10.4) * mm, "end": v(18, -17.32) * mm});
            skLineSegment(sketch, "E323.MirrorCS", {"start": v(-62, -72.75) * mm, "end": v(-62, -65.82) * mm});
            skLineSegment(sketch, "E324.MirrorCS", {"start": v(-26, -51.96) * mm, "end": v(-26, -58.89) * mm});
            skLineSegment(sketch, "E325.MirrorCS", {"start": v(-34, -38.1) * mm, "end": v(-34, -45.03) * mm});
            skLineSegment(sketch, "E326.MirrorCS", {"start": v(22, -24.25) * mm, "end": v(16, -20.78) * mm});
            skLineSegment(sketch, "E327.MirrorCS", {"start": v(18, -65.82) * mm, "end": v(18, -72.75) * mm});
            skLineSegment(sketch, "E328.MirrorCS", {"start": v(40, -34.64) * mm, "end": v(34, -38.1) * mm});
            skLineSegment(sketch, "E329.MirrorCS", {"start": v(-54, -51.96) * mm, "end": v(-48, -48.5) * mm});
            skLineSegment(sketch, "E330.MirrorCS", {"start": v(-56, -6.93) * mm, "end": v(-50, -10.4) * mm});
            skLineSegment(sketch, "E331.MirrorCS", {"start": v(26, -24.25) * mm, "end": v(26, -31.18) * mm});
            skLineSegment(sketch, "E332.MirrorCS", {"start": v(-30, -45.03) * mm, "end": v(-30, -38.1) * mm});
            skLineSegment(sketch, "E333.MirrorCS", {"start": v(-6, 3.46) * mm, "end": v(-6, -24.25) * mm, "construction": true});
            skLineSegment(sketch, "E334.MirrorCS", {"start": v(46, -17.32) * mm, "end": v(46, -10.4) * mm});
            skPoint(sketch, "E335.MirrorP", {"position": v(14, -13.86) * mm});
            skLineSegment(sketch, "E336.MirrorCS", {"start": v(-38, -31.18) * mm, "end": v(-38, -24.25) * mm});
            skLineSegment(sketch, "E337.MirrorCS", {"start": v(14, -45.03) * mm, "end": v(14, -38.1) * mm});
            skLineSegment(sketch, "E338.MirrorCS", {"start": v(42, -24.25) * mm, "end": v(42, -31.18) * mm});
            skLineSegment(sketch, "E339.MirrorCS", {"start": v(34, -65.82) * mm, "end": v(34, -72.75) * mm});
            skLineSegment(sketch, "E340.MirrorCS", {"start": v(38, -31.18) * mm, "end": v(38, -24.25) * mm});
            skLineSegment(sketch, "E341.MirrorCS", {"start": v(-54, -24.25) * mm, "end": v(-48, -20.78) * mm});
            skLineSegment(sketch, "E342.MirrorCS", {"start": v(2, -10.4) * mm, "end": v(2, -17.32) * mm});
            skLineSegment(sketch, "E343.MirrorCS", {"start": v(30, -45.03) * mm, "end": v(30, -38.1) * mm});
            skLineSegment(sketch, "E344.MirrorCS", {"start": v(6, -51.96) * mm, "end": v(0, -48.5) * mm});
            skLineSegment(sketch, "E345.MirrorCS", {"start": v(-46, -17.32) * mm, "end": v(-46, -10.4) * mm});
            skLineSegment(sketch, "E346.MirrorCS", {"start": v(-50, -45.03) * mm, "end": v(-56, -48.5) * mm});
            skLineSegment(sketch, "E347.MirrorCS", {"start": v(38, -24.25) * mm, "end": v(32, -20.78) * mm});
            skLineSegment(sketch, "E348.MirrorCS", {"start": v(50, -45.03) * mm, "end": v(56, -48.5) * mm});
            skLineSegment(sketch, "E349.MirrorCS", {"start": v(2, -38.1) * mm, "end": v(2, -45.03) * mm});
            skLineSegment(sketch, "E350.MirrorCS", {"start": v(42, -51.96) * mm, "end": v(42, -58.89) * mm});
            skLineSegment(sketch, "E351.MirrorCS", {"start": v(56, -34.64) * mm, "end": v(50, -38.1) * mm});
            skLineSegment(sketch, "E352.MirrorCS", {"start": v(30, -72.75) * mm, "end": v(30, -65.82) * mm});
            skLineSegment(sketch, "E353.MirrorCS", {"start": v(-14, -72.75) * mm, "end": v(-14, -65.82) * mm});
            skLineSegment(sketch, "E354.MirrorCS", {"start": v(-14, -45.03) * mm, "end": v(-14, -38.1) * mm});
            skLineSegment(sketch, "E355.MirrorCS", {"start": v(2, -45.03) * mm, "end": v(8, -48.5) * mm});
            skLineSegment(sketch, "E356.MirrorCS", {"start": v(-22, -58.89) * mm, "end": v(-22, -51.96) * mm});
            skLineSegment(sketch, "E357.MirrorCS", {"start": v(6, -31.18) * mm, "end": v(6, -24.25) * mm});
            skLineSegment(sketch, "E358.MirrorCS", {"start": v(38, -51.96) * mm, "end": v(32, -48.5) * mm});
            skLineSegment(sketch, "E359.MirrorCS", {"start": v(-46, -72.75) * mm, "end": v(-46, -65.82) * mm});
            skLineSegment(sketch, "E360.MirrorCS", {"start": v(34, -45.03) * mm, "end": v(40, -48.5) * mm});
            skLineSegment(sketch, "E361.MirrorCS", {"start": v(34, -10.4) * mm, "end": v(34, -17.32) * mm});
            skLineSegment(sketch, "E362.MirrorCS", {"start": v(8, -62.35) * mm, "end": v(2, -65.82) * mm});
            skLineSegment(sketch, "E363.MirrorCS", {"start": v(14, -72.75) * mm, "end": v(14, -65.82) * mm});
            skLineSegment(sketch, "E364.MirrorCS", {"start": v(0, 0) * mm, "end": v(-8, -13.86) * mm, "construction": true});
            skLineSegment(sketch, "E365.MirrorCS", {"start": v(-42, -24.25) * mm, "end": v(-42, -31.18) * mm});
            skLineSegment(sketch, "E366.MirrorCS", {"start": v(50, -72.75) * mm, "end": v(56, -76.21) * mm});
            skLineSegment(sketch, "E367.MirrorCS", {"start": v(-30, -72.75) * mm, "end": v(-30, -65.82) * mm});
            skLineSegment(sketch, "E368.MirrorCS", {"start": v(-16, -48.5) * mm, "end": v(-10, -51.96) * mm});
            skLineSegment(sketch, "E369.MirrorCS", {"start": v(2, -72.75) * mm, "end": v(8, -76.21) * mm});
            skLineSegment(sketch, "E370.MirrorCS", {"start": v(40, -6.93) * mm, "end": v(34, -10.4) * mm});
            skLineSegment(sketch, "E371.MirrorCS", {"start": v(6, -24.25) * mm, "end": v(0, -20.78) * mm});
            skLineSegment(sketch, "E372.MirrorCS", {"start": v(18, -17.32) * mm, "end": v(24, -20.78) * mm});
            skLineSegment(sketch, "E373.MirrorCS", {"start": v(22, -58.89) * mm, "end": v(22, -51.96) * mm});
            skLineSegment(sketch, "E374.MirrorCS", {"start": v(26, -51.96) * mm, "end": v(26, -58.89) * mm});
            skLineSegment(sketch, "E375.MirrorCS", {"start": v(-10, -31.18) * mm, "end": v(-16, -34.64) * mm});
            skLineSegment(sketch, "E376.MirrorCS", {"start": v(-62, -17.32) * mm, "end": v(-62, -10.4) * mm});
            skLineSegment(sketch, "E377.MirrorCS", {"start": v(-34, -10.4) * mm, "end": v(-34, -17.32) * mm});
            skLineSegment(sketch, "E378.MirrorCS", {"start": v(-56, -62.35) * mm, "end": v(-50, -65.82) * mm});
            skLineSegment(sketch, "E379.MirrorCS", {"start": v(-38, -58.89) * mm, "end": v(-38, -51.96) * mm});
            skLineSegment(sketch, "E380.MirrorCS", {"start": v(22, -31.18) * mm, "end": v(22, -24.25) * mm});
            skLineSegment(sketch, "E381.MirrorCS", {"start": v(50, -10.4) * mm, "end": v(50, -17.32) * mm});
            skLineSegment(sketch, "E382.MirrorCS", {"start": v(50, -17.32) * mm, "end": v(56, -20.78) * mm});
            skLineSegment(sketch, "E383.MirrorCS", {"start": v(-2, -38.1) * mm, "end": v(-2, -45.03) * mm});
            skLineSegment(sketch, "E384.MirrorCS", {"start": v(-48.5, 70.75) * mm, "end": v(-48.5, -70.75) * mm});
            skCircle(sketch, "E385.MirrorC", {"center": v(8, -13.86) * mm, "radius": 6 * mm, "construction": true});
            skLineSegment(sketch, "E386.MirrorCS", {"start": v(-54, -58.89) * mm, "end": v(-54, -51.96) * mm});
            skSolve(sketch);
        }
        {
            var Q0;
            Q0=makeQuery(id+"F0.imprint","IMPRINT",FACE,{"disambiguationData":[TD([[makeQuery(id+"F0.imprint","IMPRINT",EDGE,{"derivedFrom":sQuery(id+"F0.wireOp",EDGE,"E1.0")}),1.0]])]});
            extrude(context, id + "F1", {"entities" : qUnion([Q0]), "depth" : 3 * mm});
        }
    });
